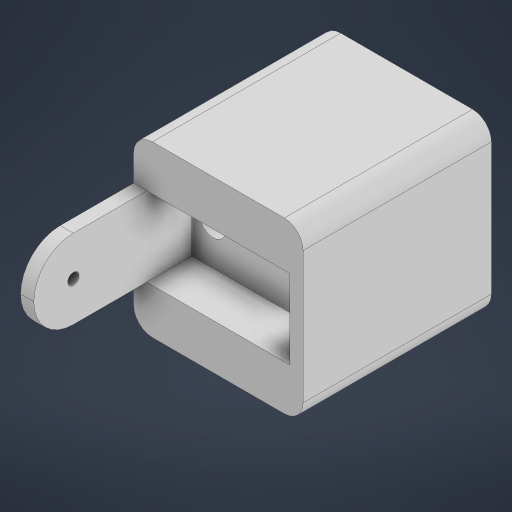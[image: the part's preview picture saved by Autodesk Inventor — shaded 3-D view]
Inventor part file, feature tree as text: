
AUTODESK INVENTOR PART (.ipt)
format: ipt  version: 2023 (Build 270158000, 158)  size: 237,568 bytes
history: native  units: mm
features: extrude x7, sketch x7, fillet x2
ambient origin geometry x8: Origin, YZ Plane, XZ Plane, XY Plane, X Axis, Y Axis, Z Axis, Center Point
bodies: Solid1 (feature_tree)
feature tree (16):
  extrude  "Extrusion1"  Depth=45.0mm
  fillet  "Fillet1"  Radius=50.0mm
  extrude  "Extrusion2"  Depth=5.0mm
  extrude  "Extrusion3"  Depth=20.0mm TaperAngle=0.0deg
  extrude  "Extrusion4"  Depth=12.0mm
  extrude  "Extrusion5"  Depth=21.0mm
  extrude  "Extrusion6"  Depth=12.0mm
  fillet  "Fillet2"  Radius=4.0mm
  extrude  "Extrusion7"  Depth=7.0mm
  sketch  "Sketch1"  dims[d0=45.0mm d1=45.0mm d2=50.0mm d3=0.0mm]
  sketch  "Sketch2"  dims[d4=5.0mm d5=22.5mm]
  sketch  "Sketch3"  dims[d6=15.0mm d7=20.0mm d8=0.0mm]
  sketch  "Sketch4"  dims[d11=3.5mm d12=12.0mm]
  sketch  "Sketch5"  dims[d13=38.0mm d14=21.0mm]
  sketch  "Sketch6"  dims[d15=12.0mm d16=0.0mm d20=26.0mm d21=4.0mm]
  sketch  "Sketch7"  dims[d22=7.0mm d23=0.0mm d24=7.0mm d25=40.0mm d26=0.0mm d27=30.0mm d28=0.0mm d29=10.5mm d30=3.0mm d31=30.0mm d32=0.0mm d17=0.5mm d18=0.872665mm]
